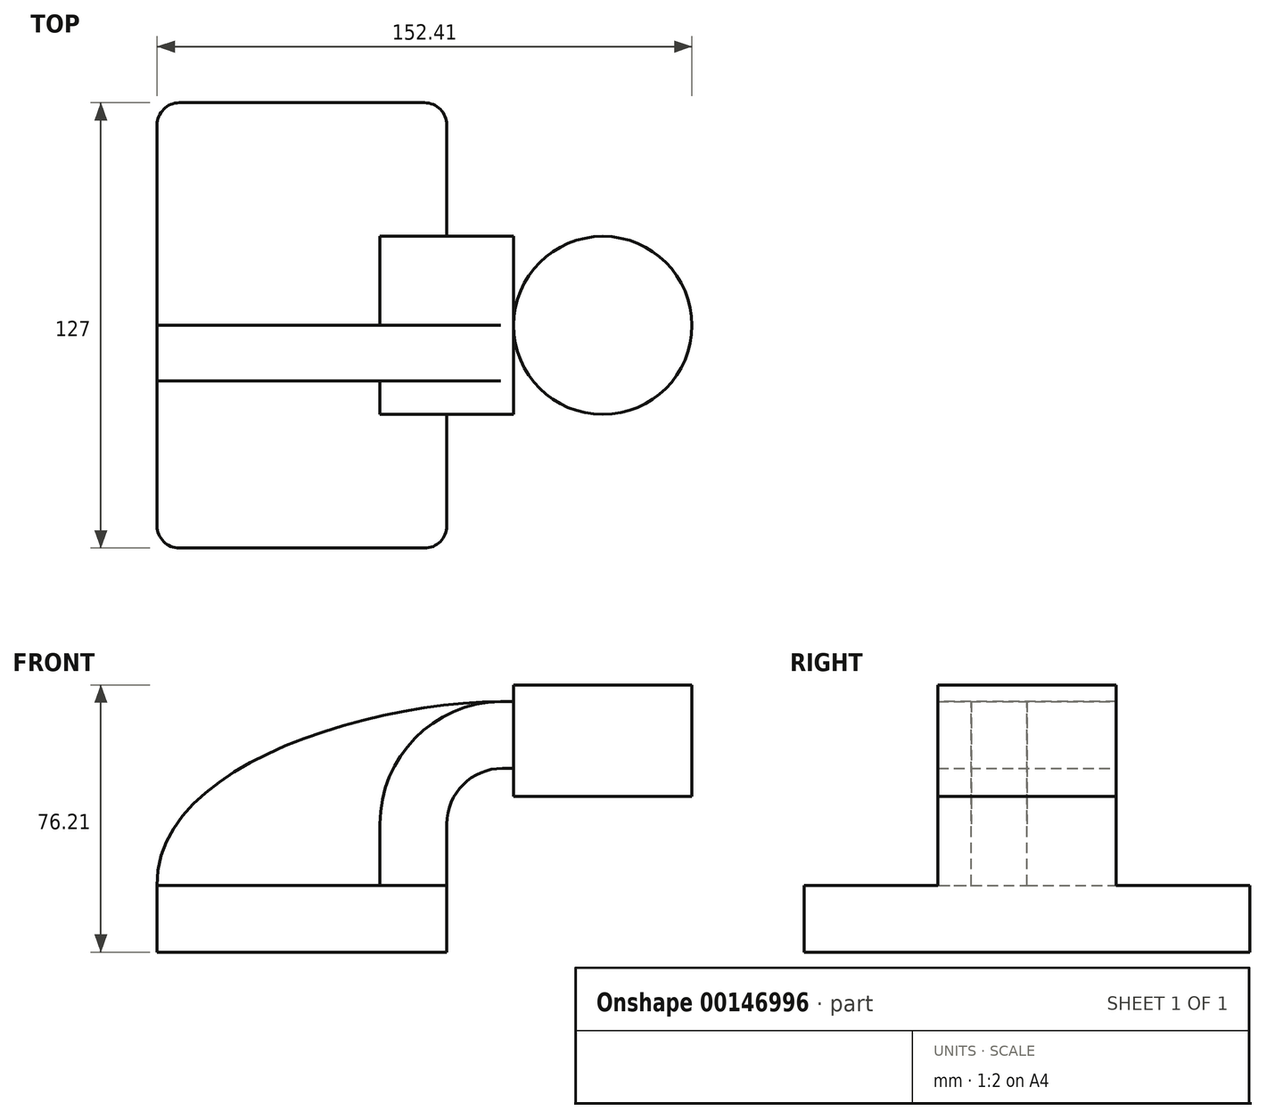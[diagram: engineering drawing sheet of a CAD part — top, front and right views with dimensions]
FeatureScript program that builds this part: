
annotation { "Feature Type Name" : "Feature", "Feature Type Description" : "" }
export const myFeature = defineFeature(function(context is Context, id is Id, definition is map)
    precondition{}
    {
        {
            var Q0;
            Q0=qCreatedBy(makeId("Front.planeOp"),FACE);
            var sketch = newSketch(context, id + "F0", { "sketchPlane" : qUnion([Q0])});
            skLineSegment(sketch, "E0.bottom", {"start": v(-41.28, 9.52) * mm, "end": v(41.28, 9.53) * mm});
            skLineSegment(sketch, "E0.top", {"start": v(-41.28, -9.53) * mm, "end": v(41.28, -9.53) * mm});
            skLineSegment(sketch, "E0.left", {"start": v(-41.28, 9.52) * mm, "end": v(-41.28, -9.53) * mm});
            skLineSegment(sketch, "E0.right", {"start": v(41.28, 9.53) * mm, "end": v(41.28, -9.52) * mm});
            skPoint(sketch, "E0.middle", {"position": v(0, 0) * mm});
            skLineSegment(sketch, "E1.bottom", {"start": v(111.13, 34.93) * mm, "end": v(60.33, 34.93) * mm});
            skLineSegment(sketch, "E1.top", {"start": v(111.13, 66.68) * mm, "end": v(60.33, 66.68) * mm});
            skLineSegment(sketch, "E1.left", {"start": v(111.13, 34.93) * mm, "end": v(111.13, 66.68) * mm});
            skLineSegment(sketch, "E1.right", {"start": v(60.33, 34.93) * mm, "end": v(60.33, 66.68) * mm});
            skPoint(sketch, "E1.middle", {"position": v(85.72, 50.8) * mm});
            skLineSegment(sketch, "E2", {"start": v(41.27, 9.53) * mm, "end": v(41.27, 27) * mm});
            skArc(sketch, "E3", {"start": v(41.27, 27) * mm, "mid": v(45.92, 38.23) * mm, "end": v(57.15, 42.88) * mm});
            skLineSegment(sketch, "E4", {"start": v(57.15, 42.88) * mm, "end": v(85.6, 42.88) * mm});
            skLineSegment(sketch, "E5.0", {"start": v(57.15, 61.93) * mm, "end": v(85.72, 61.93) * mm});
            skArc(sketch, "E5.1", {"start": v(22.23, 27) * mm, "mid": v(32.45, 51.7) * mm, "end": v(57.15, 61.93) * mm});
            skLineSegment(sketch, "E5.2", {"start": v(22.22, 9.53) * mm, "end": v(22.22, 27) * mm});
            skLineSegment(sketch, "E6", {"start": v(85.72, 34.93) * mm, "end": v(85.72, 66.68) * mm});
            skFitSpline(sketch, "E7", {"points": [v(-41.28, 9.52) * mm, v(57.15, 61.93) * mm], "startDerivative": vector(-2.27, 101.28) * mm, "endDerivative": vector(117.15, 0.72) * mm});
            skSolve(sketch);
        }
        {
            var Q0;
            Q0=makeQuery(id+"F0.imprint","IMPRINT",FACE,{"disambiguationData":[TD([[makeQuery(id+"F0.imprint","IMPRINT",EDGE,{"derivedFrom":sQuery(id+"F0.wireOp",EDGE,"E0.top")}),1.0]])]});
            extrude(context, id + "F1", {"entities" : qUnion([Q0]), "endBound" : BoundingType.SYMMETRIC, "depth" : 127 * mm});
        }
        {
            var Q0;
            {var subQ5=sQuery(id+"F0.wireOp",EDGE,"E2");Q0=makeQuery(id+"F0.imprint","IMPRINT",FACE,{"disambiguationData":[TD([[makeQuery(id+"F0.imprint","IMPRINT",EDGE,{"derivedFrom":subQ5}),1.0]])]});}
            extrude(context, id + "F2", {"entities" : qUnion([Q0]), "operationType" : NewBodyOperationType.ADD, "endBound" : BoundingType.SYMMETRIC, "depth" : 50.8 * mm});
        }
        {
            var Q0;
            {var subQ3=sQuery(id+"F0.wireOp",EDGE,"E5.2");Q0=makeQuery(id+"F0.imprint","IMPRINT",FACE,{"disambiguationData":[TD([[makeQuery(id+"F0.imprint","IMPRINT",EDGE,{"derivedFrom":subQ3}),1.0]])]});}
            extrude(context, id + "F3", {"entities" : qUnion([Q0]), "operationType" : NewBodyOperationType.ADD, "depth" : 15.88 * mm});
        }
        {
            var Q0;
            {var subQ0=sQuery(id+"F0.wireOp",EDGE,"E1.left");Q0=makeQuery(id+"F0.imprint","IMPRINT",FACE,{"disambiguationData":[TD([[makeQuery(id+"F0.imprint","IMPRINT",EDGE,{"derivedFrom":subQ0}),1.0]])]});}
            var Q1;
            Q1=sQuery(id+"F0.wireOp",EDGE,"E6");
            revolve(context, id + "F4", {"operationType" : NewBodyOperationType.ADD, "entities" : qUnion([Q0]), "axis" : qUnion([Q1]), "revolveType" : RevolveType.FULL});
        }
        {
            var Q0;
            Q0=makeQuery(id+"F1.opExtrude","CAP_EDGE",EDGE,{"disambiguationData":[OSD([sQuery(id+"F0.wireOp",EDGE,"E0.right")])],"isStart":true});
            var Q1;
            Q1=makeQuery(id+"F1.opExtrude","CAP_EDGE",EDGE,{"disambiguationData":[OSD([sQuery(id+"F0.wireOp",EDGE,"E0.left")])],"isStart":true});
            var Q2;
            Q2=makeQuery(id+"F1.opExtrude","CAP_EDGE",EDGE,{"disambiguationData":[OSD([sQuery(id+"F0.wireOp",EDGE,"E0.left")])],"isStart":false});
            var Q3;
            Q3=makeQuery(id+"F1.opExtrude","CAP_EDGE",EDGE,{"disambiguationData":[OSD([sQuery(id+"F0.wireOp",EDGE,"E0.right")])],"isStart":false});
            fillet(context, id + "F5", {"entities" : qUnion([Q0, Q1, Q2, Q3]), "radius" : 6.35 * mm, "tangentPropagation" : true, "allowEdgeOverflow" : false});
        }
    });
